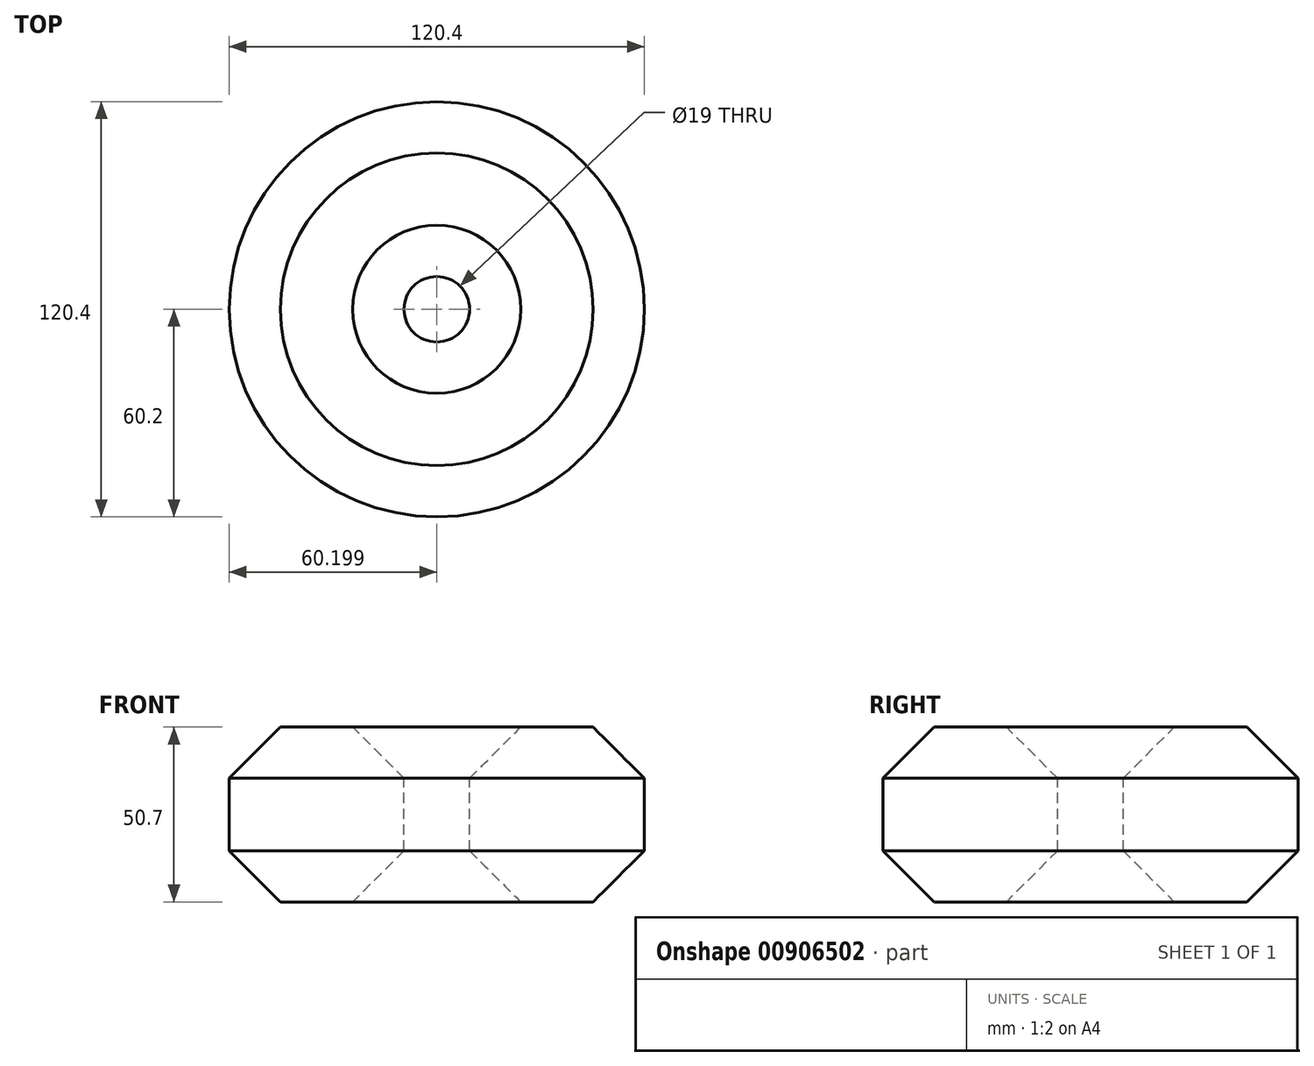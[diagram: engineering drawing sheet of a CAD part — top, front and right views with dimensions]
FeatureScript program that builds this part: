
annotation { "Feature Type Name" : "Feature", "Feature Type Description" : "" }
export const myFeature = defineFeature(function(context is Context, id is Id, definition is map)
    precondition{}
    {
        {
            var Q0;
            Q0=qCreatedBy(makeId("Front.planeOp"),FACE);
            var sketch = newSketch(context, id + "F0", { "sketchPlane" : qUnion([Q0])});
            skLineSegment(sketch, "E0.0", {"start": v(0, 23.63) * mm, "end": v(10.5, 23.63) * mm});
            skLineSegment(sketch, "E0.1", {"start": v(10.5, 23.63) * mm, "end": v(25.35, 8.78) * mm});
            skLineSegment(sketch, "E0.2", {"start": v(25.35, 8.78) * mm, "end": v(25.35, -12.22) * mm});
            skLineSegment(sketch, "E0.3", {"start": v(25.35, -12.22) * mm, "end": v(10.5, -27.07) * mm});
            skLineSegment(sketch, "E0.4", {"start": v(10.5, -27.07) * mm, "end": v(-10.5, -27.07) * mm});
            skLineSegment(sketch, "E0.5", {"start": v(-10.5, -27.07) * mm, "end": v(-25.35, -12.22) * mm});
            skLineSegment(sketch, "E0.6", {"start": v(-25.35, -12.22) * mm, "end": v(-25.35, 8.78) * mm});
            skLineSegment(sketch, "E0.7", {"start": v(-25.35, 8.78) * mm, "end": v(-10.5, 23.63) * mm});
            skPoint(sketch, "E0.0.midPoint", {"position": v(0, 23.63) * mm});
            skPoint(sketch, "E0.cCircle.center.orphan", {"position": v(0, -1.72) * mm});
            skLineSegment(sketch, "E1", {"start": v(-10.5, 23.63) * mm, "end": v(0, 23.63) * mm});
            skPoint(sketch, "E2.orphan", {"position": v(25.35, 25.47) * mm});
            skLineSegment(sketch, "E3", {"start": v(34.85, 8.78) * mm, "end": v(34.85, -21.99) * mm});
            skSolve(sketch);
        }
        {
            var Q0;
            Q0=makeQuery(id+"F0.imprint","IMPRINT",FACE,{"disambiguationData":[TD([[makeQuery(id+"F0.imprint","IMPRINT",EDGE,{"derivedFrom":sQuery(id+"F0.wireOp",EDGE,"E0.0")}),-1.0]])]});
            var Q1;
            Q1=sQuery(id+"F0.wireOp",EDGE,"E3");
            revolve(context, id + "F1", {"surfaceOperationType" : NewSurfaceOperationType.NEW, "entities" : qUnion([Q0]), "axis" : qUnion([Q1]), "revolveType" : RevolveType.FULL});
        }
    });
